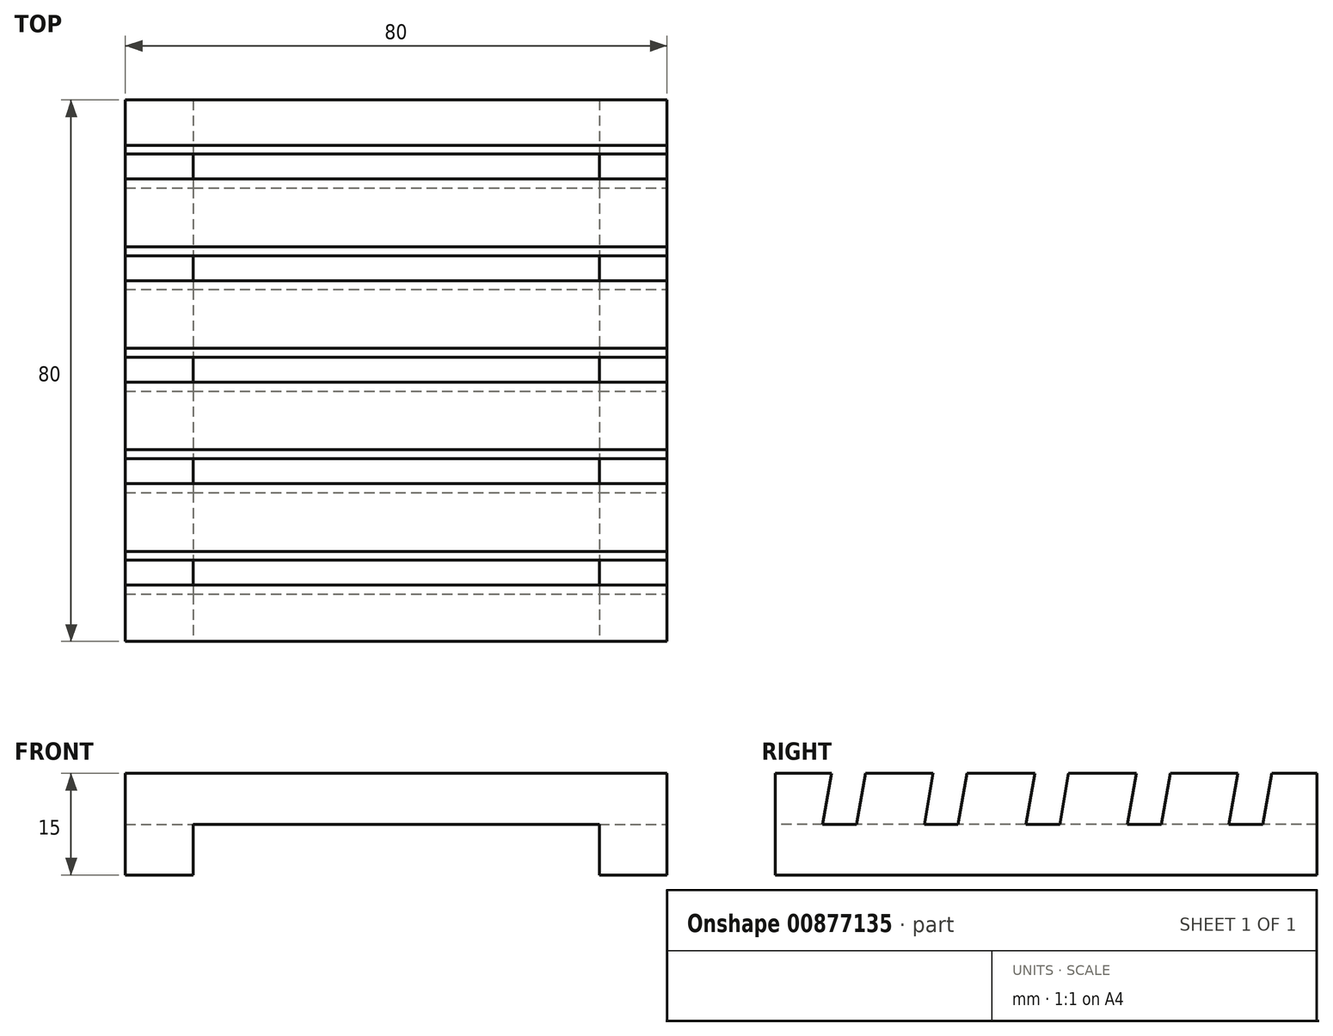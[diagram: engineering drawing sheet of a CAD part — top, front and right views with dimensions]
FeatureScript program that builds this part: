
annotation { "Feature Type Name" : "Feature", "Feature Type Description" : "" }
export const myFeature = defineFeature(function(context is Context, id is Id, definition is map)
    precondition{}
    {
        {
            var Q0;
            Q0=qCreatedBy(makeId("Top.planeOp"),FACE);
            var sketch = newSketch(context, id + "F0", { "sketchPlane" : qUnion([Q0])});
            skLineSegment(sketch, "E0.bottom", {"start": v(40, -40) * mm, "end": v(-40, -40) * mm});
            skLineSegment(sketch, "E0.top", {"start": v(40, 40) * mm, "end": v(-40, 40) * mm});
            skLineSegment(sketch, "E0.left", {"start": v(40, -40) * mm, "end": v(40, 40) * mm});
            skLineSegment(sketch, "E0.right", {"start": v(-40, -40) * mm, "end": v(-40, 40) * mm});
            skPoint(sketch, "E0.middle", {"position": v(0, 0) * mm});
            skSolve(sketch);
        }
        {
            var Q0;
            Q0=makeQuery(id+"F0.imprint","IMPRINT",FACE,{"disambiguationData":[TD([[makeQuery(id+"F0.imprint","IMPRINT",EDGE,{"derivedFrom":sQuery(id+"F0.wireOp",EDGE,"E0.bottom")}),-1.0]])]});
            extrude(context, id + "F1", {"entities" : qUnion([Q0]), "depth" : 15 * mm, "offsetDistance" : 25 * mm});
        }
        {
            var Q0;
            Q0=makeQuery(id+"F1.opExtrude","SWEPT_FACE",FACE,{"disambiguationData":[OSD([sQuery(id+"F0.wireOp",EDGE,"E0.left")])]});
            var sketch = newSketch(context, id + "F2", { "sketchPlane" : qUnion([Q0])});
            skLineSegment(sketch, "E1", {"start": v(-40, 7.5) * mm, "end": v(40, 7.5) * mm, "construction": true});
            skLineSegment(sketch, "E2", {"start": v(-31.68, 15) * mm, "end": v(-33, 7.5) * mm});
            skLineSegment(sketch, "E3", {"start": v(-33, 7.5) * mm, "end": v(-28, 7.5) * mm});
            skLineSegment(sketch, "E4", {"start": v(-28, 7.5) * mm, "end": v(-26.68, 15) * mm});
            skLineSegment(sketch, "E5", {"start": v(-26.68, 15) * mm, "end": v(-31.68, 15) * mm});
            skLineSegment(sketch, "E6", {"start": v(-28, 7.5) * mm, "end": v(-18, 7.5) * mm, "construction": true});
            skLineSegment(sketch, "E7", {"start": v(-16.68, 15) * mm, "end": v(-18, 7.5) * mm});
            skLineSegment(sketch, "E8", {"start": v(-18, 7.5) * mm, "end": v(-13, 7.5) * mm});
            skLineSegment(sketch, "E9", {"start": v(-13, 7.5) * mm, "end": v(-11.68, 15) * mm});
            skLineSegment(sketch, "E10", {"start": v(-11.68, 15) * mm, "end": v(-16.68, 15) * mm});
            skLineSegment(sketch, "E11", {"start": v(-13, 7.5) * mm, "end": v(-3, 7.5) * mm, "construction": true});
            skLineSegment(sketch, "E12", {"start": v(13.32, 15) * mm, "end": v(12, 7.5) * mm});
            skLineSegment(sketch, "E13", {"start": v(12, 7.5) * mm, "end": v(17, 7.5) * mm});
            skLineSegment(sketch, "E14", {"start": v(17, 7.5) * mm, "end": v(18.32, 15) * mm});
            skLineSegment(sketch, "E15", {"start": v(18.32, 15) * mm, "end": v(13.32, 15) * mm});
            skLineSegment(sketch, "E16", {"start": v(17, 7.5) * mm, "end": v(27, 7.5) * mm, "construction": true});
            skLineSegment(sketch, "E17", {"start": v(-1.68, 15) * mm, "end": v(-3, 7.5) * mm});
            skLineSegment(sketch, "E18", {"start": v(-3, 7.5) * mm, "end": v(2, 7.5) * mm});
            skLineSegment(sketch, "E19", {"start": v(2, 7.5) * mm, "end": v(3.32, 15) * mm});
            skLineSegment(sketch, "E20", {"start": v(3.32, 15) * mm, "end": v(-1.68, 15) * mm});
            skLineSegment(sketch, "E21", {"start": v(2, 7.5) * mm, "end": v(12, 7.5) * mm, "construction": true});
            skLineSegment(sketch, "E22", {"start": v(28.32, 15) * mm, "end": v(27, 7.5) * mm});
            skLineSegment(sketch, "E23", {"start": v(27, 7.5) * mm, "end": v(32, 7.5) * mm});
            skLineSegment(sketch, "E24", {"start": v(32, 7.5) * mm, "end": v(33.32, 15) * mm});
            skLineSegment(sketch, "E25", {"start": v(33.32, 15) * mm, "end": v(28.32, 15) * mm});
            skLineSegment(sketch, "E26", {"start": v(32, 7.5) * mm, "end": v(42, 7.5) * mm, "construction": true});
            skLineSegment(sketch, "E27", {"start": v(-33, 7.5) * mm, "end": v(-40, 7.5) * mm, "construction": true});
            skSolve(sketch);
        }
        {
            var Q0;
            Q0=makeQuery(id+"F2.imprint","IMPRINT",FACE,{"disambiguationData":[TD([[makeQuery(id+"F2.imprint","IMPRINT",EDGE,{"derivedFrom":sQuery(id+"F2.wireOp",EDGE,"E2")}),1.0]])]});
            var Q1;
            Q1=makeQuery(id+"F2.imprint","IMPRINT",FACE,{"disambiguationData":[TD([[makeQuery(id+"F2.imprint","IMPRINT",EDGE,{"derivedFrom":sQuery(id+"F2.wireOp",EDGE,"E7")}),1.0]])]});
            var Q2;
            Q2=makeQuery(id+"F2.imprint","IMPRINT",FACE,{"disambiguationData":[TD([[makeQuery(id+"F2.imprint","IMPRINT",EDGE,{"derivedFrom":sQuery(id+"F2.wireOp",EDGE,"E17")}),1.0]])]});
            var Q3;
            Q3=makeQuery(id+"F2.imprint","IMPRINT",FACE,{"disambiguationData":[TD([[makeQuery(id+"F2.imprint","IMPRINT",EDGE,{"derivedFrom":sQuery(id+"F2.wireOp",EDGE,"E12")}),1.0]])]});
            var Q4;
            Q4=makeQuery(id+"F2.imprint","IMPRINT",FACE,{"disambiguationData":[TD([[makeQuery(id+"F2.imprint","IMPRINT",EDGE,{"derivedFrom":sQuery(id+"F2.wireOp",EDGE,"E22")}),1.0]])]});
            extrude(context, id + "F3", {"entities" : qUnion([Q0, Q1, Q2, Q3, Q4]), "operationType" : NewBodyOperationType.REMOVE, "oppositeDirection" : true, "depth" : 111 * mm, "offsetDistance" : 25 * mm});
        }
        {
            var Q0;
            Q0=makeQuery(id+"F1.opExtrude","SWEPT_FACE",FACE,{"disambiguationData":[OSD([sQuery(id+"F0.wireOp",EDGE,"E0.bottom")])]});
            var sketch = newSketch(context, id + "F4", { "sketchPlane" : qUnion([Q0])});
            skLineSegment(sketch, "E28", {"start": v(-40, 7.5) * mm, "end": v(40, 7.5) * mm, "construction": true});
            skLineSegment(sketch, "E29", {"start": v(-40, 7.5) * mm, "end": v(-30, 7.5) * mm, "construction": true});
            skLineSegment(sketch, "E30", {"start": v(40, 7.5) * mm, "end": v(30, 7.5) * mm, "construction": true});
            skLineSegment(sketch, "E31", {"start": v(-30, 7.5) * mm, "end": v(30, 7.5) * mm});
            skLineSegment(sketch, "E32", {"start": v(30, 7.5) * mm, "end": v(30, 0) * mm});
            skLineSegment(sketch, "E33", {"start": v(-30, 7.5) * mm, "end": v(-30, 0) * mm});
            skSolve(sketch);
        }
        {
            var Q0;
            Q0=makeQuery(id+"F4.imprint","IMPRINT",FACE,{"disambiguationData":[TD([[makeQuery(id+"F4.imprint","IMPRINT",EDGE,{"derivedFrom":sQuery(id+"F4.wireOp",EDGE,"E31")}),-1.0]])]});
            extrude(context, id + "F5", {"entities" : qUnion([Q0]), "operationType" : NewBodyOperationType.REMOVE, "oppositeDirection" : true, "depth" : 111 * mm, "offsetDistance" : 25 * mm});
        }
    });
